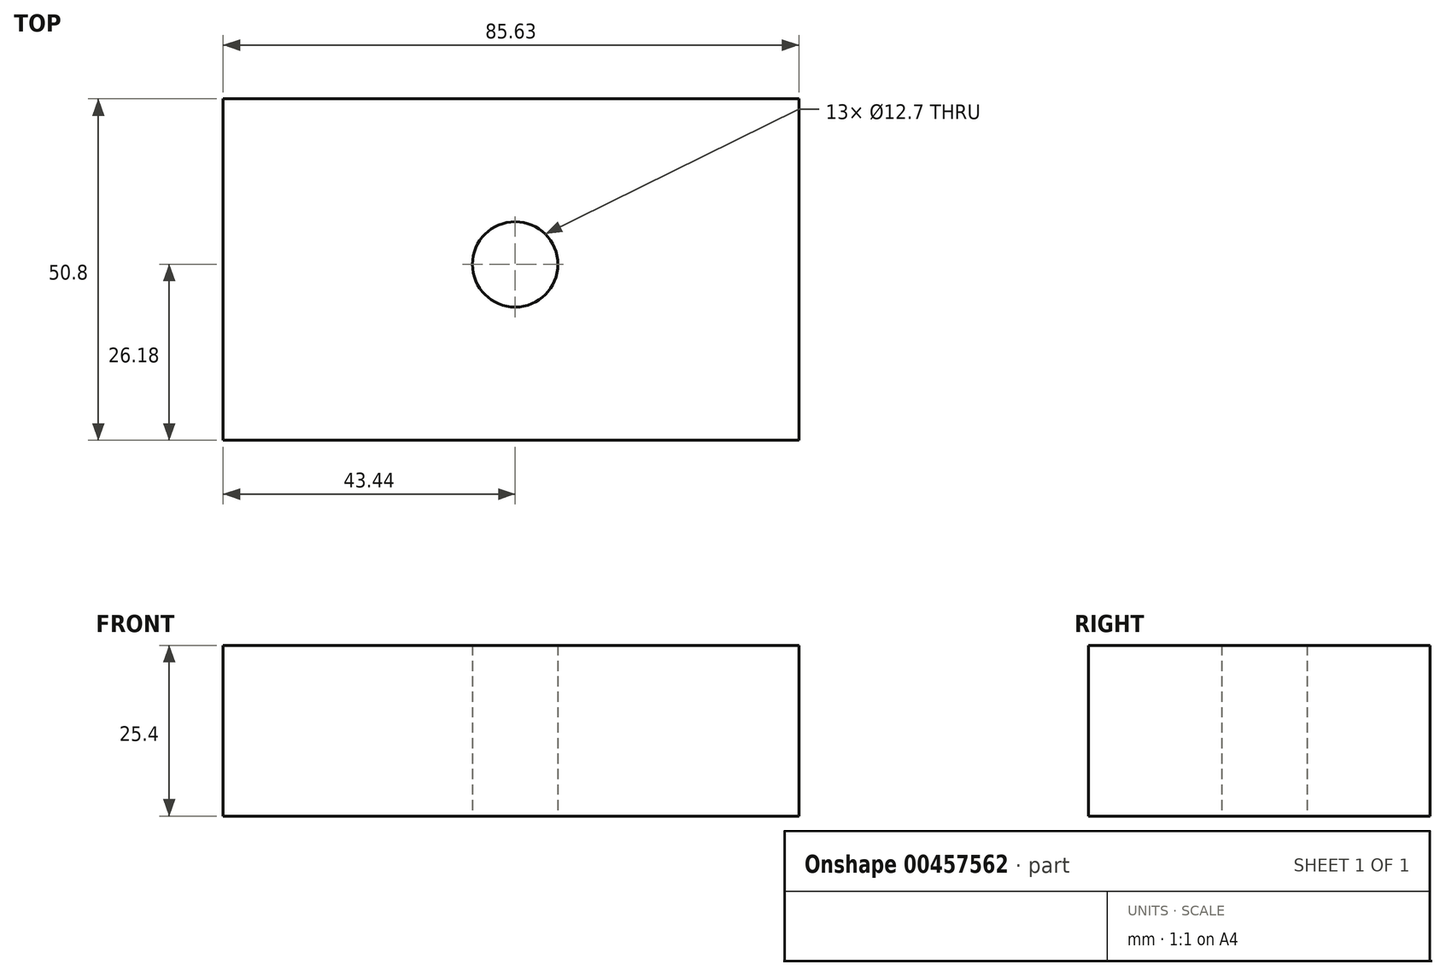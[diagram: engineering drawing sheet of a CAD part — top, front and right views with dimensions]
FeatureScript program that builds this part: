
annotation { "Feature Type Name" : "Feature", "Feature Type Description" : "" }
export const myFeature = defineFeature(function(context is Context, id is Id, definition is map)
    precondition{}
    {
        {
            var Q0;
            Q0=qCreatedBy(makeId("Top.planeOp"),FACE);
            var sketch = newSketch(context, id + "F0", { "sketchPlane" : qUnion([Q0])});
            skLineSegment(sketch, "E0.bottom", {"start": v(-43.44, 24.62) * mm, "end": v(42.2, 24.62) * mm});
            skLineSegment(sketch, "E0.top", {"start": v(-43.44, -26.18) * mm, "end": v(42.2, -26.18) * mm});
            skLineSegment(sketch, "E0.left", {"start": v(-43.44, 24.62) * mm, "end": v(-43.44, -26.18) * mm});
            skLineSegment(sketch, "E0.right", {"start": v(42.2, 24.62) * mm, "end": v(42.2, -26.18) * mm});
            skCircle(sketch, "E1", {"center": v(0, 0) * mm, "radius": 6.35 * mm});
            skSolve(sketch);
        }
        {
            var Q0;
            Q0 = qSketchRegion(id + "F0", true);
            extrude(context, id + "F1", {"entities" : qUnion([Q0]), "depth" : 25.4 * mm});
        }
    });
